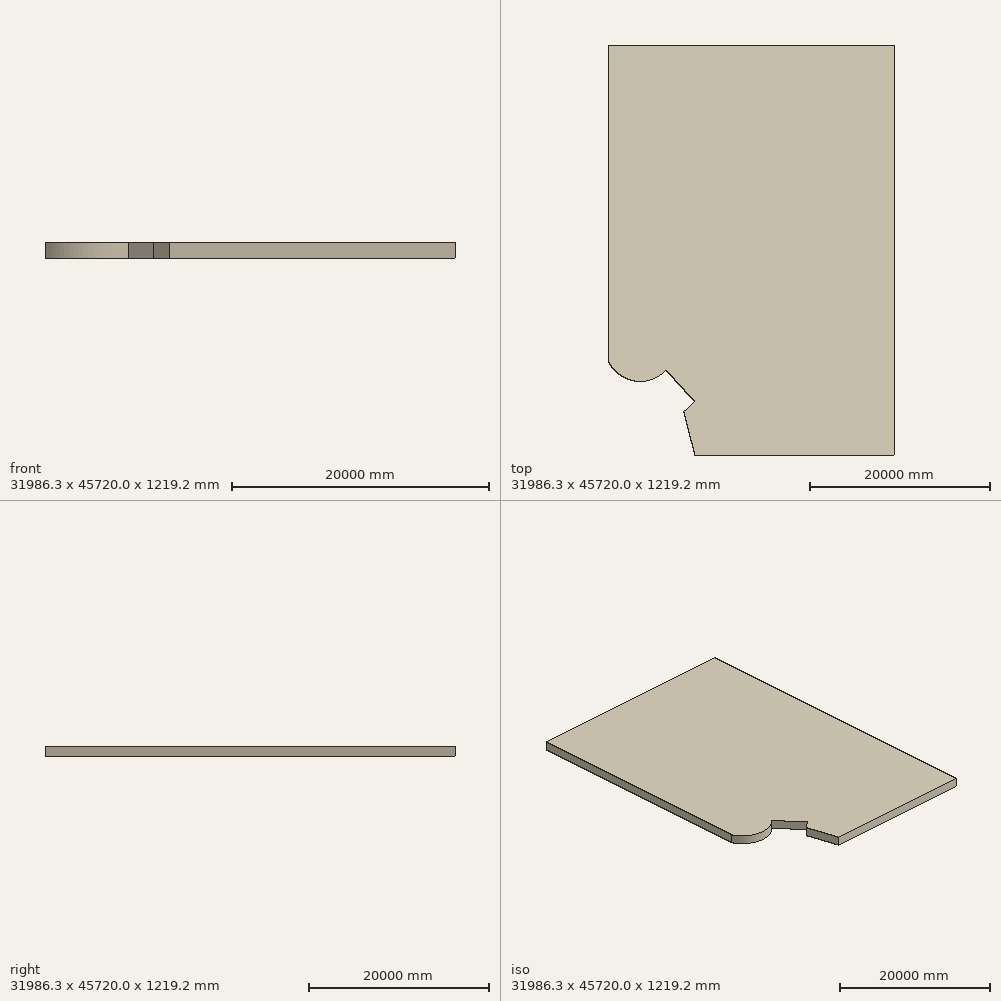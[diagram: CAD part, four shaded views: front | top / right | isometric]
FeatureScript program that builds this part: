
annotation { "Feature Type Name" : "Feature", "Feature Type Description" : "" }
export const myFeature = defineFeature(function(context is Context, id is Id, definition is map)
    precondition{}
    {
        {
            var Q0;
            Q0=qCreatedBy(makeId("Top.planeOp"),FACE);
            var sketch = newSketch(context, id + "F0", { "sketchPlane" : qUnion([Q0])});
            skLineSegment(sketch, "E0.bottom", {"start": v(0, 0) * mm, "end": v(31986.28, 0) * mm});
            skLineSegment(sketch, "E0.top", {"start": v(13203.62, -45720) * mm, "end": v(31986.28, -45720) * mm});
            skLineSegment(sketch, "E0.left", {"start": v(0, 0) * mm, "end": v(0, -35113.77) * mm});
            skLineSegment(sketch, "E0.right", {"start": v(31986.28, 0) * mm, "end": v(31986.28, -45720) * mm});
            skLineSegment(sketch, "E1", {"start": v(9687.04, -39740.84) * mm, "end": v(6477.9, -36214.7) * mm});
            skArc(sketch, "E2", {"start": v(0, -35113.77) * mm, "mid": v(2941.54, -37414.19) * mm, "end": v(6477.9, -36214.7) * mm});
            skLineSegment(sketch, "E3", {"start": v(9687.04, -39740.84) * mm, "end": v(8448.37, -40868.16) * mm});
            skLineSegment(sketch, "E4", {"start": v(8448.37, -40868.16) * mm, "end": v(9687.04, -45720) * mm});
            skLineSegment(sketch, "E5", {"start": v(9687.04, -45720) * mm, "end": v(13203.62, -45720) * mm});
            skSolve(sketch);
        }
        {
            var Q0;
            Q0 = qSketchRegion(id + "F0", true);
            extrude(context, id + "F1", {"entities" : qUnion([Q0]), "depth" : 1219.2 * mm, "offsetDistance" : 30.48 * mm});
        }
    });
